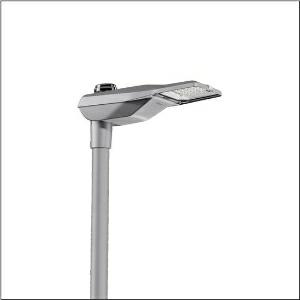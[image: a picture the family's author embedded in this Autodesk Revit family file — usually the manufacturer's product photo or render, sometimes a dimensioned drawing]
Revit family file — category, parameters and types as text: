
# Revit family: streetlight_sl_21_micro___st1_0a_5xe5d57n08db_813c
name_source: partatom
category: Lighting Fixtures
units: mm (PartAtom-declared; Revit-internal decimal feet)

## family parameters
Cut with Voids When Loaded = No
Host = Face
Light Source = No
Part Type = Normal
Room Calculation Point = No
Round Connector Dimension = Use Diameter
Shared = No

## types (1)
- --- (1 x LED, 4400 lm, 39.1 W, 3000K)
    Apparent Load = 39 VA
    CIE Flux Codes = 37 72 97 100 100
    Color Rendering = 80
    Color Temperature = 3000K
    Default Elevation = 1800 mm
    Description = Streetlight SL 21 micro, mast luminaire, primary light control with lens, of PMMA, primary optical cover: cover, of toughened safety glass, transparent, light distribution: ST1.0a, light emission: direct distribution, primary light characteristic: asymmetric, installation type: post-top, LED, 3G 1.5mm², High Power LED, rated luminous flux: 4.400lm, luminous efficacy: 113lm/W, light colour: 830, colour temperature: 3000K, control gear: NEMA (7pin), control: overheat protection, pre-setting: linear dimming characteristic, constant luminous flux control, time-dependent luminous flux control, flexible luminous flux parameterisation, mains connection: 230..240V, AC, 50/60Hz, connection cable pre-assembled, cable length: 6,5m, wiring characteristics: H07RN-F, start of lifetime: 39W, end of service life: 41W, reduction: 18W, luminaire housing, of diecast aluminium (EN AC-44300), powder-coated, Siteco® metallic grey (DB 702S), corrosivity category C5 mid according to DIN EN ISO 12944, multi-level sealing system, sealing non-destructively replaceable, inclination adjustable: 0°, 5°, 10°, 15°, length: 528mm, width: 235mm, height: 110mm, spigot size: 76/60mm (post-top), mounting height: 4..8m, protection rating (complete): IP66, insulation class (complete): insulation class I (protective earthing), certification: CE, ENEC, ENEC+, VDE, impact resistance: IK10, permissible operating ambient temperature for outdoor applications: -40..+50°C, standard-compliant lighting for roads and squares, packaging unit: 1 piece

Light Distribution: ST1.0a
    Height = 110 mm
    Lamp = 1 x LED
    Lamp Light Flux = 4400 lm
    Lamp Power = 39.1 W
    Lamp count = 1
    Length = 528 mm
    Luminous efficacy = 113 lm/W
    Manufacturer = Siteco
    ModVariant = No
    Model = 5XE5D57N08DB
    Number of Poles = 1
    OnlyDefault = Yes
    Power Factor = 1
    Product Name = Streetlight SL 21 micro | ST1.0a
    Product group = mast luminaire | pylon top
    ProductGroupID = 6100
    Protection Class = Protection class I
    Protection Degree = IP 66
    RLX_Detail_Level = 1
    RLX_Emergency_Light_Flux = 0 lm
    RLX_Emergency_Type = 0
    RLX_Emergency_Type_DB = No
    RlxData = <blob elided: 98421 chars, md5=608011fc>
    Socket = socket
    Standby Power = 0 W
    System Light Flux = 4400 lm
    System Power = 39 W
    Type Comments = factory setting: luminous flux: 100 % | dim-lin: 254 | 765 mA
    Type Image = l_1294375.jpg
    URL = http://relux.com
    VarID = @adj_136438
    Voltage = 0 V
    Weight = 0.00 kg
    Width = 235 mm

## geometry (parser evidence)
native form markers: Blend x4, Sweep x10
no freeform markers — native parametric forms only
